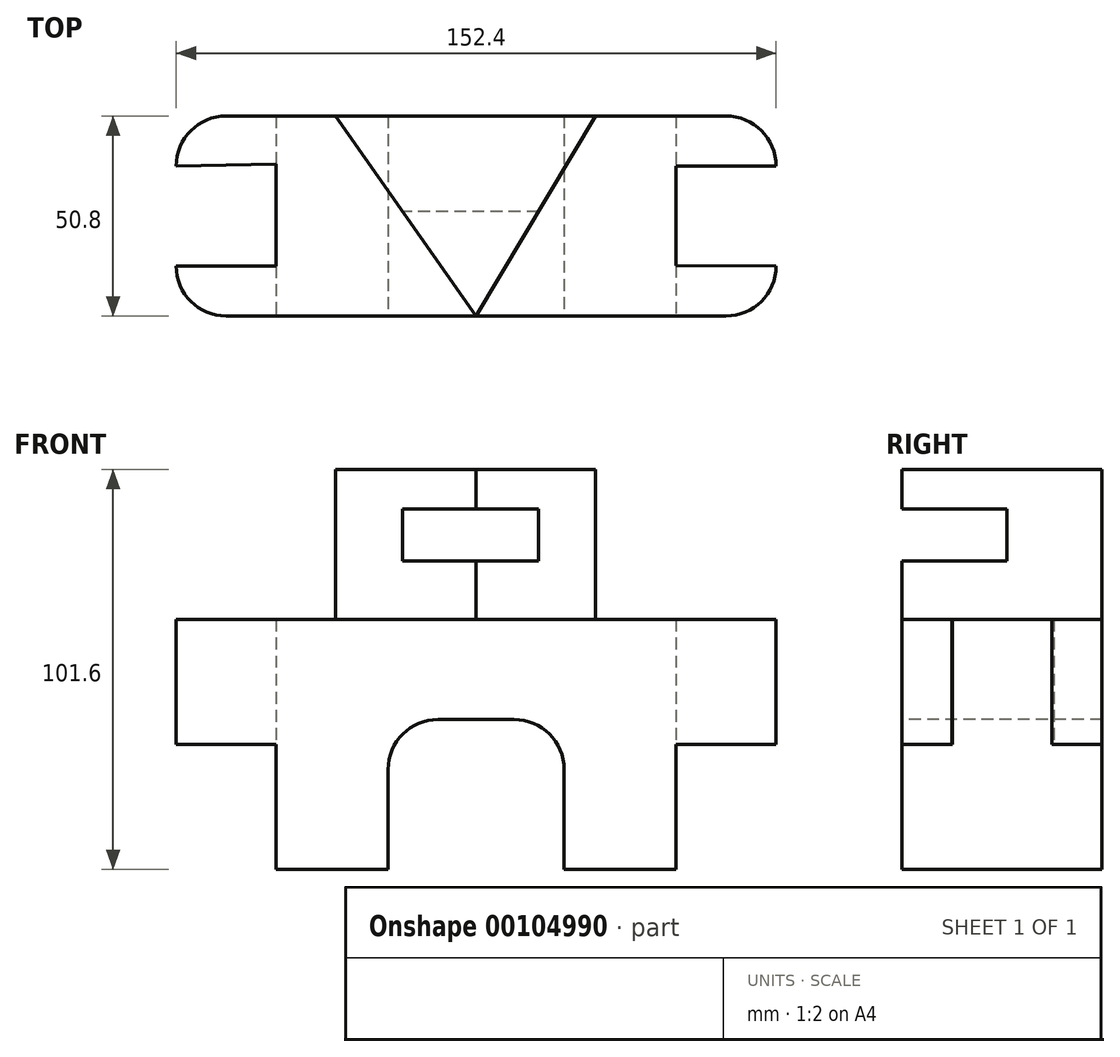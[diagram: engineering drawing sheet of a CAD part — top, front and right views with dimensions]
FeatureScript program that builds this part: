
annotation { "Feature Type Name" : "Feature", "Feature Type Description" : "" }
export const myFeature = defineFeature(function(context is Context, id is Id, definition is map)
    precondition{}
    {
        {
            var Q0;
            Q0=qCreatedBy(makeId("Front.planeOp"),FACE);
            var sketch = newSketch(context, id + "F0", { "sketchPlane" : qUnion([Q0])});
            skLineSegment(sketch, "E0.bottom", {"start": v(25.4, 0) * mm, "end": v(53.85, 0) * mm});
            skLineSegment(sketch, "E0.left", {"start": v(0, 31.75) * mm, "end": v(0, 63.5) * mm});
            skLineSegment(sketch, "E0.right", {"start": v(152.4, 31.75) * mm, "end": v(152.4, 63.5) * mm});
            skLineSegment(sketch, "E1.top", {"start": v(0, 63.5) * mm, "end": v(152.4, 63.5) * mm});
            skLineSegment(sketch, "E2.top", {"start": v(25.4, 63.5) * mm, "end": v(63.5, 63.5) * mm});
            skLineSegment(sketch, "E2.left", {"start": v(25.4, 0) * mm, "end": v(25.4, 31.75) * mm});
            skLineSegment(sketch, "E3.bottom", {"start": v(88.9, 63.5) * mm, "end": v(127, 63.5) * mm});
            skLineSegment(sketch, "E3.top", {"start": v(98.55, 0) * mm, "end": v(127, 0) * mm});
            skLineSegment(sketch, "E3.left", {"start": v(127, 31.75) * mm, "end": v(127, 0) * mm});
            skLineSegment(sketch, "E4.bottom", {"start": v(88.9, 63.5) * mm, "end": v(152.4, 63.5) * mm});
            skLineSegment(sketch, "E4.top", {"start": v(127, 31.75) * mm, "end": v(152.4, 31.75) * mm});
            skLineSegment(sketch, "E4.right", {"start": v(152.4, 63.5) * mm, "end": v(152.4, 31.75) * mm});
            skLineSegment(sketch, "E5.bottom", {"start": v(0, 63.5) * mm, "end": v(38.1, 63.5) * mm});
            skLineSegment(sketch, "E5.top", {"start": v(0, 31.75) * mm, "end": v(25.4, 31.75) * mm});
            skLineSegment(sketch, "E5.left", {"start": v(0, 63.5) * mm, "end": v(0, 31.75) * mm});
            skLineSegment(sketch, "E6", {"start": v(53.85, 0) * mm, "end": v(53.85, 25.4) * mm});
            skLineSegment(sketch, "E7", {"start": v(98.55, 0) * mm, "end": v(98.55, 25.4) * mm});
            skLineSegment(sketch, "E8", {"start": v(66.55, 38.1) * mm, "end": v(85.85, 38.1) * mm});
            skPoint(sketch, "E9.visualSharp", {"position": v(53.85, 38.1) * mm});
            skArc(sketch, "E9.filletArc", {"start": v(66.55, 38.1) * mm, "mid": v(57.57, 34.38) * mm, "end": v(53.85, 25.4) * mm});
            skPoint(sketch, "E10.visualSharp", {"position": v(98.55, 38.1) * mm});
            skArc(sketch, "E10.filletArc", {"start": v(98.55, 25.4) * mm, "mid": v(94.83, 34.38) * mm, "end": v(85.85, 38.1) * mm});
            skPoint(sketch, "E11.orphan", {"position": v(152.4, 127) * mm});
            skPoint(sketch, "E12.orphan", {"position": v(152.4, 0) * mm});
            skPoint(sketch, "E13.orphan", {"position": v(0, 0) * mm});
            skSolve(sketch);
        }
        {
            var Q0;
            Q0=qCreatedBy(makeId("Top.planeOp"),FACE);
            var sketch = newSketch(context, id + "F1", { "sketchPlane" : qUnion([Q0])});
            skLineSegment(sketch, "E14.left", {"start": v(0, 12.7) * mm, "end": v(0, 38.1) * mm});
            skLineSegment(sketch, "E14.right", {"start": v(152.4, 12.7) * mm, "end": v(152.4, 38.1) * mm});
            skPoint(sketch, "E15.visualSharp", {"position": v(0, 50.8) * mm});
            skArc(sketch, "E15.filletArc", {"start": v(12.7, 50.8) * mm, "mid": v(3.72, 47.08) * mm, "end": v(0, 38.1) * mm});
            skPoint(sketch, "E16.visualSharp", {"position": v(0, 0) * mm});
            skArc(sketch, "E16.filletArc", {"start": v(0, 12.7) * mm, "mid": v(3.72, 3.72) * mm, "end": v(12.7, 0) * mm});
            skPoint(sketch, "E17.visualSharp", {"position": v(152.4, 0) * mm});
            skArc(sketch, "E17.filletArc", {"start": v(139.7, 0) * mm, "mid": v(148.68, 3.72) * mm, "end": v(152.4, 12.7) * mm});
            skPoint(sketch, "E18.visualSharp", {"position": v(152.4, 50.8) * mm});
            skArc(sketch, "E18.filletArc", {"start": v(152.4, 38.1) * mm, "mid": v(148.68, 47.08) * mm, "end": v(139.7, 50.8) * mm});
            skLineSegment(sketch, "E19", {"start": v(0, 50.8) * mm, "end": v(0, 38.1) * mm});
            skLineSegment(sketch, "E20", {"start": v(0, 50.8) * mm, "end": v(12.7, 50.8) * mm});
            skLineSegment(sketch, "E21", {"start": v(0, 12.7) * mm, "end": v(0, 0) * mm});
            skLineSegment(sketch, "E22", {"start": v(0, 0) * mm, "end": v(12.7, 0) * mm});
            skLineSegment(sketch, "E23", {"start": v(0, 38.1) * mm, "end": v(0, 12.7) * mm});
            skLineSegment(sketch, "E24", {"start": v(152.4, 38.1) * mm, "end": v(152.4, 12.7) * mm});
            skLineSegment(sketch, "E25", {"start": v(139.7, 0) * mm, "end": v(152.4, 0) * mm});
            skLineSegment(sketch, "E26", {"start": v(152.4, 0) * mm, "end": v(152.4, 12.7) * mm});
            skLineSegment(sketch, "E27", {"start": v(152.4, 38.1) * mm, "end": v(152.4, 50.8) * mm});
            skLineSegment(sketch, "E28", {"start": v(139.7, 50.8) * mm, "end": v(152.4, 50.8) * mm});
            skLineSegment(sketch, "E29", {"start": v(0, 12.7) * mm, "end": v(25.4, 12.7) * mm});
            skLineSegment(sketch, "E30", {"start": v(25.4, 12.7) * mm, "end": v(25.4, 38.57) * mm});
            skLineSegment(sketch, "E31", {"start": v(25.4, 38.57) * mm, "end": v(0, 38.1) * mm});
            skLineSegment(sketch, "E32", {"start": v(152.4, 38.1) * mm, "end": v(127, 38.1) * mm});
            skLineSegment(sketch, "E33", {"start": v(127, 38.1) * mm, "end": v(127, 12.82) * mm});
            skLineSegment(sketch, "E34", {"start": v(127, 12.82) * mm, "end": v(152.4, 12.7) * mm});
            skSolve(sketch);
        }
        {
            var Q0;
            Q0 = qSketchRegion(id + "F0", true);
            extrude(context, id + "F2", {"entities" : qUnion([Q0]), "oppositeDirection" : true, "depth" : 50.8 * mm});
        }
        {
            var Q0;
            Q0 = qSketchRegion(id + "F1", true);
            extrude(context, id + "F3", {"entities" : qUnion([Q0]), "operationType" : NewBodyOperationType.REMOVE, "depth" : 63.5 * mm});
        }
        {
            var Q0;
            Q0=qCreatedBy(makeId("Top.planeOp"),FACE);
            var sketch = newSketch(context, id + "F4", { "sketchPlane" : qUnion([Q0])});
            skLineSegment(sketch, "E35", {"start": v(76.2, 0) * mm, "end": v(40.46, 50.8) * mm});
            skLineSegment(sketch, "E36", {"start": v(40.46, 50.8) * mm, "end": v(106.5, 50.8) * mm});
            skLineSegment(sketch, "E37", {"start": v(106.5, 50.8) * mm, "end": v(76.2, 0) * mm});
            skSolve(sketch);
        }
        {
            var Q0;
            Q0 = qSketchRegion(id + "F4", true);
            extrude(context, id + "F5", {"entities" : qUnion([Q0]), "operationType" : NewBodyOperationType.ADD, "depth" : 101.6 * mm, "hasSecondDirection" : true, "secondDirectionOppositeDirection" : false, "secondDirectionDepth" : 38.1 * mm});
        }
        {
            var Q0;
            Q0=qCreatedBy(makeId("Right.planeOp"),FACE);
            var sketch = newSketch(context, id + "F6", { "sketchPlane" : qUnion([Q0])});
            skLineSegment(sketch, "E38.bottom", {"start": v(0, 91.52) * mm, "end": v(26.6, 91.52) * mm});
            skLineSegment(sketch, "E38.top", {"start": v(0, 78.4) * mm, "end": v(26.6, 78.4) * mm});
            skLineSegment(sketch, "E38.left", {"start": v(0, 91.52) * mm, "end": v(0, 78.4) * mm});
            skLineSegment(sketch, "E38.right", {"start": v(26.6, 91.52) * mm, "end": v(26.6, 78.4) * mm});
            skSolve(sketch);
        }
        {
            var Q0;
            Q0 = qSketchRegion(id + "F6", true);
            extrude(context, id + "F7", {"entities" : qUnion([Q0]), "operationType" : NewBodyOperationType.REMOVE, "endBound" : BoundingType.THROUGH_ALL, "depth" : 101.6 * mm});
        }
    });
